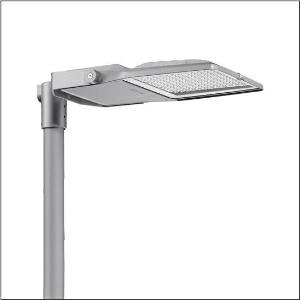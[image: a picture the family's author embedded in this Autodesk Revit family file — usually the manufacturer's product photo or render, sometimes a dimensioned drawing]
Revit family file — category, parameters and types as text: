
# Revit family: floodlight_fl_21_iq_midi___pl43_5xa7781f4a3a_cde7
name_source: partatom
category: Lighting Fixtures
units: mm (PartAtom-declared; Revit-internal decimal feet)

## family parameters
Cut with Voids When Loaded = No
Host = Face
Light Source = No
Part Type = Normal
Room Calculation Point = No
Round Connector Dimension = Use Diameter
Shared = No

## types (1)
- --- (1 x LED, 38290 lm, 270.2 W, 4000K)
    Apparent Load = 270 VA
    CIE Flux Codes = 27 78 99 100 100
    Color Rendering = 70
    Color Temperature = 4000K
    Default Elevation = 1800 mm
    Description = Floodlight FL 21 iQ midi, floodlight, primary light control with lens, of PMMA, primary optical cover: protective disc, of toughened safety glass, transparent, light distribution: PL43, light emission: direct distribution, installation type: surface-mounted, lamps: LED, High Power LED, rated values: 38.290lm | 270,2W | 141,7lm/W (begin service life); end service life: 38.290lm | 286,6W; at 50% lumin. flux: 19.145lm | 117,7W | 162,7lm/W, colour temperature: 4000K, colour rendering: CRI > 70, light colour: 740, light setting 1 begin service life: 100% | 38.290lm | 270,2W | 141,7lm/W | 4.000K, light setting 1 end service life: 286,6W, further light settings possible, control: optimised constant luminous flux control (CLO 2.0), Desk-Remote (wireless, voltage-free reading and setting of iQ features in the workshop via application-optimized NFC function/RFID function), Light-Fading, Smart-Wire, Night-Set, Lumen-Switch, Temp-Guard, Auto-Match, pre-setting: linear dimming characteristic, with terminal, 6-pole, mains connection: 220..240V, AC, 50/60Hz, luminaire housing, of diecast aluminium, powder-coated, SITECO metallic grey (DB 702S), corrosivity category C5 mid according to DIN EN ISO 12944suitable for swimming poolschlorine-resistant, sealing non-destructively replaceable, please order mast flange separately, mast bracket, of steel, galvanised, powder-coated, SITECO metallic grey (DB 702S), protection rating (complete): IP66, insulation class (complete): insulation class II (safety insulation), certification: CE, ENEC, VDE, protection symbol: D, impact resistance: IK08, permissible operating ambient temperature: -40..+40°C, permissible operating ambient temperature for outdoor applications: -40..+50°C, standard: DIN EN 12944, LABS conformity tested according to VDMA 24364:2018-05, packaging unit: 1 piece

Light Distribution: PL43
    Height = 76 mm
    Lamp = 1 x LED
    Lamp Light Flux = 38290 lm
    Lamp Power = 270.2 W
    Lamp count = 1
    Length = 657 mm
    Luminous efficacy = 142 lm/W
    Manufacturer = Siteco
    ModVariant = No
    Model = 5XA7781F4A3A
    Mounting Place = Pole
    Mounting Type = Pole annexe
    Number of Poles = 1
    OnlyDefault = Yes
    Power Factor = 1
    Product Name = Floodlight FL 21 iQ midi | PL43
    Product group = floodlight | pylon annexe
    ProductGroupID = 6201
    Protection Class = Protection class II
    Protection Degree = IP 66
    RLX_Detail_Level = 1
    RLX_Emergency_Light_Flux = 0 lm
    RLX_Emergency_Type = 0
    RLX_Emergency_Type_DB = No
    RlxData = <blob elided: 153897 chars, md5=a28c0c89>
    Socket = socket
    Standby Power = 0 W
    System Light Flux = 38290 lm
    System Power = 270 W
    Type Comments = factory setting: luminous flux: 100 % | dim-lin: 254 | 620 mA
    Type Image = l_1007123.jpg
    URL = http://relux.com
    VarID = @adj_106313
    Voltage = 0 V
    Weight = 0.00 kg
    Width = 442 mm

## geometry (parser evidence)
native form markers: Blend x4, Sweep x13
no freeform markers — native parametric forms only
